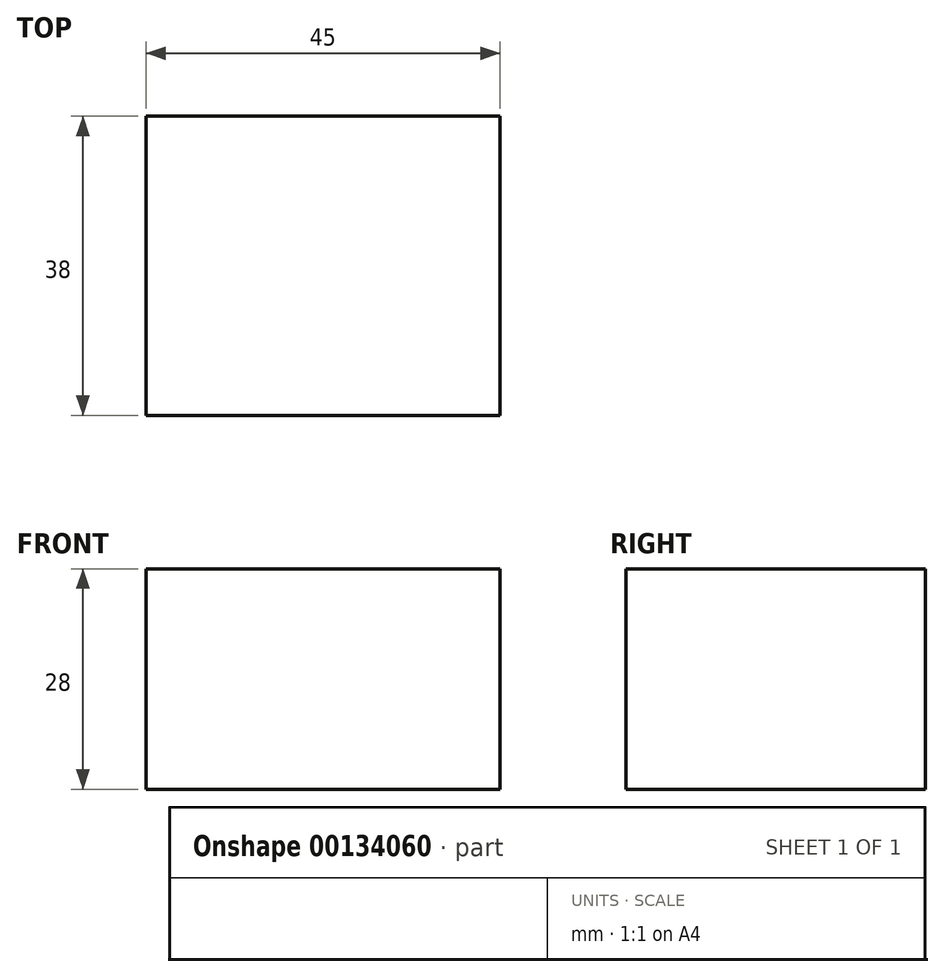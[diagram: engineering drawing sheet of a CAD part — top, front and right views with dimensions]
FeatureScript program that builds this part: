
annotation { "Feature Type Name" : "Feature", "Feature Type Description" : "" }
export const myFeature = defineFeature(function(context is Context, id is Id, definition is map)
    precondition{}
    {
        {
            var Q0;
            Q0=qCreatedBy(makeId("Top.planeOp"),FACE);
            var sketch = newSketch(context, id + "F0", { "sketchPlane" : qUnion([Q0])});
            skLineSegment(sketch, "E0.bottom", {"start": v(22.5, 19) * mm, "end": v(-22.5, 19) * mm});
            skLineSegment(sketch, "E0.top", {"start": v(22.5, -19) * mm, "end": v(-22.5, -19) * mm});
            skLineSegment(sketch, "E0.left", {"start": v(22.5, 19) * mm, "end": v(22.5, -19) * mm});
            skLineSegment(sketch, "E0.right", {"start": v(-22.5, 19) * mm, "end": v(-22.5, -19) * mm});
            skPoint(sketch, "E0.middle", {"position": v(0, 0) * mm});
            skSolve(sketch);
        }
        {
            var Q0;
            Q0 = qSketchRegion(id + "F0", true);
            extrude(context, id + "F1", {"entities" : qUnion([Q0]), "depth" : 28 * mm});
        }
    });
